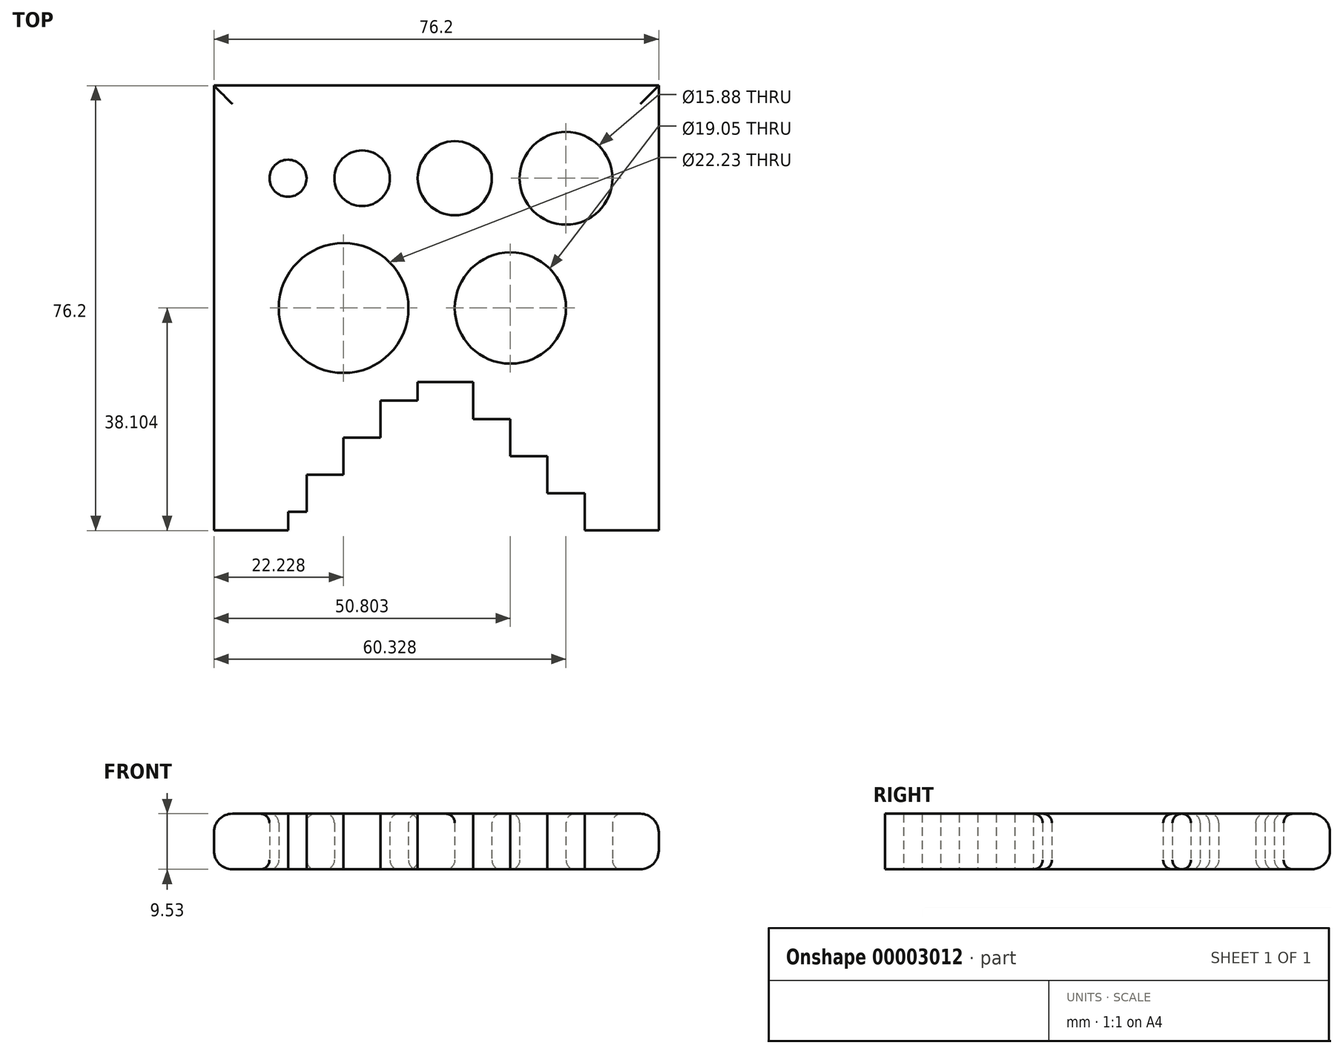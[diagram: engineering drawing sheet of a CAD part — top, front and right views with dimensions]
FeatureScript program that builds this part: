
annotation { "Feature Type Name" : "Feature", "Feature Type Description" : "" }
export const myFeature = defineFeature(function(context is Context, id is Id, definition is map)
    precondition{}
    {
        {
            var Q0;
            Q0=qCreatedBy(makeId("Top.planeOp"),FACE);
            var sketch = newSketch(context, id + "F0", { "sketchPlane" : qUnion([Q0])});
            skLineSegment(sketch, "E0.bottom", {"start": v(-53.47, 47.93) * mm, "end": v(22.73, 47.93) * mm});
            skLineSegment(sketch, "E0.top", {"start": v(-53.47, -28.27) * mm, "end": v(-40.77, -28.27) * mm});
            skLineSegment(sketch, "E0.left", {"start": v(-53.47, 47.93) * mm, "end": v(-53.47, -28.27) * mm});
            skLineSegment(sketch, "E0.right", {"start": v(22.73, 47.93) * mm, "end": v(22.73, -28.27) * mm});
            skLineSegment(sketch, "E1", {"start": v(-40.77, -25.1) * mm, "end": v(-37.6, -25.1) * mm});
            skLineSegment(sketch, "E2", {"start": v(-37.6, -18.74) * mm, "end": v(-31.24, -18.74) * mm});
            skLineSegment(sketch, "E3", {"start": v(-31.24, -12.4) * mm, "end": v(-24.9, -12.4) * mm});
            skLineSegment(sketch, "E4", {"start": v(-24.9, -6.04) * mm, "end": v(-18.54, -6.04) * mm});
            skLineSegment(sketch, "E5", {"start": v(-18.54, -2.87) * mm, "end": v(-9.02, -2.87) * mm});
            skLineSegment(sketch, "E6", {"start": v(3.68, -21.92) * mm, "end": v(10.03, -21.92) * mm});
            skLineSegment(sketch, "E7", {"start": v(-2.67, -15.57) * mm, "end": v(3.68, -15.57) * mm});
            skLineSegment(sketch, "E8", {"start": v(-9.02, -9.22) * mm, "end": v(-2.67, -9.22) * mm});
            skLineSegment(sketch, "E9", {"start": v(-18.54, -6.04) * mm, "end": v(-18.54, -2.87) * mm});
            skLineSegment(sketch, "E10", {"start": v(-24.9, -12.4) * mm, "end": v(-24.9, -6.04) * mm});
            skLineSegment(sketch, "E11", {"start": v(-31.24, -18.74) * mm, "end": v(-31.24, -12.4) * mm});
            skLineSegment(sketch, "E12", {"start": v(-37.6, -25.1) * mm, "end": v(-37.6, -18.74) * mm});
            skLineSegment(sketch, "E13", {"start": v(-40.77, -28.27) * mm, "end": v(-40.77, -25.1) * mm});
            skLineSegment(sketch, "E14", {"start": v(-9.02, -9.22) * mm, "end": v(-9.02, -2.87) * mm});
            skLineSegment(sketch, "E15", {"start": v(-2.67, -15.57) * mm, "end": v(-2.67, -9.22) * mm});
            skLineSegment(sketch, "E16", {"start": v(3.68, -21.92) * mm, "end": v(3.68, -15.57) * mm});
            skLineSegment(sketch, "E17", {"start": v(10.03, -28.27) * mm, "end": v(10.03, -21.92) * mm});
            skPoint(sketch, "E18.orphan", {"position": v(-15.37, -2.87) * mm});
            skPoint(sketch, "E19.orphan", {"position": v(-53.47, -25.1) * mm});
            skPoint(sketch, "E20.orphan", {"position": v(-53.47, -18.74) * mm});
            skPoint(sketch, "E21.orphan", {"position": v(-53.47, -12.4) * mm});
            skPoint(sketch, "E22.orphan", {"position": v(-53.47, -6.04) * mm});
            skPoint(sketch, "E23.orphan", {"position": v(22.73, -15.57) * mm});
            skPoint(sketch, "E24.orphan", {"position": v(22.73, -21.92) * mm});
            skPoint(sketch, "E25.orphan", {"position": v(22.73, -2.87) * mm});
            skPoint(sketch, "E26.orphan", {"position": v(-53.47, -2.87) * mm});
            skLineSegment(sketch, "E27.trimOffspring", {"start": v(10.03, -28.27) * mm, "end": v(22.73, -28.27) * mm});
            skLineSegment(sketch, "E28", {"start": v(-53.47, 32.06) * mm, "end": v(22.73, 32.06) * mm, "construction": true});
            skCircle(sketch, "E29", {"center": v(-40.77, 32.06) * mm, "radius": 3.18 * mm});
            skCircle(sketch, "E30", {"center": v(-28.07, 32.06) * mm, "radius": 4.76 * mm});
            skCircle(sketch, "E31", {"center": v(-12.2, 32.06) * mm, "radius": 6.35 * mm});
            skCircle(sketch, "E32", {"center": v(6.86, 32.06) * mm, "radius": 7.94 * mm});
            skLineSegment(sketch, "E33", {"start": v(22.73, 9.83) * mm, "end": v(-53.47, 9.83) * mm, "construction": true});
            skCircle(sketch, "E34", {"center": v(-2.67, 9.83) * mm, "radius": 9.53 * mm});
            skCircle(sketch, "E35", {"center": v(-31.24, 9.83) * mm, "radius": 11.11 * mm});
            skSolve(sketch);
        }
        {
            var Q0;
            {var subQ2=sQuery(id+"F0.wireOp",EDGE,"E0.right");var subQ8=sQuery(id+"F0.wireOp",EDGE,"E0.bottom");var subQ10=makeQuery(id+"F0.imprint","INTERSECT",VERTEX,{"derivedFrom":[subQ8,subQ2]});Q0=makeQuery(id+"F0.imprint","IMPRINT",FACE,{"disambiguationData":[TD([[makeQuery(id+"F0.imprint","IMPRINT",EDGE,{"disambiguationData":[TD([[subQ10,1.0]])],"derivedFrom":subQ8}),-1.0]])]});}
            var sketch = newSketch(context, id + "F1", { "sketchPlane" : qUnion([Q0])});
            skSolve(sketch);
        }
        {
            var Q0;
            Q0=makeQuery(id+"F1.imprint","IMPRINT",FACE,{"disambiguationData":[TD([[makeQuery(id+"F1.imprint","IMPRINT",EDGE,{"derivedFrom":makeQuery(id+"F0.imprint","IMPRINT",EDGE,{"derivedFrom":sQuery(id+"F0.wireOp",EDGE,"E0.bottom")})}),-1.0]])]});
            extrude(context, id + "F2", {"entities" : qUnion([Q0]), "depth" : 9.52 * mm});
        }
        {
            var Q0;
            Q0=makeQuery(id+"F2.opExtrude","CAP_EDGE",EDGE,{"disambiguationData":[OSD([sQuery(id+"F0.wireOp",EDGE,"E0.bottom")])],"isStart":false});
            var Q1;
            Q1=makeQuery(id+"F2.opExtrude","CAP_EDGE",EDGE,{"disambiguationData":[OSD([sQuery(id+"F0.wireOp",EDGE,"E0.right")])],"isStart":false});
            var Q2;
            Q2=makeQuery(id+"F2.opExtrude","CAP_EDGE",EDGE,{"disambiguationData":[OSD([sQuery(id+"F0.wireOp",EDGE,"E0.left")])],"isStart":false});
            var Q3;
            Q3=makeQuery(id+"F2.opExtrude","CAP_EDGE",EDGE,{"disambiguationData":[OSD([sQuery(id+"F0.wireOp",EDGE,"E0.right")])],"isStart":true});
            var Q4;
            Q4=makeQuery(id+"F2.opExtrude","CAP_EDGE",EDGE,{"disambiguationData":[OSD([sQuery(id+"F0.wireOp",EDGE,"E0.bottom")])],"isStart":true});
            var Q5;
            Q5=makeQuery(id+"F2.opExtrude","CAP_EDGE",EDGE,{"disambiguationData":[OSD([sQuery(id+"F0.wireOp",EDGE,"E0.left")])],"isStart":true});
            fillet(context, id + "F3", {"entities" : qUnion([Q0, Q1, Q2, Q3, Q4, Q5]), "radius" : 3.17 * mm, "tangentPropagation" : true, "allowEdgeOverflow" : false});
        }
        {
            var Q0;
            Q0=makeQuery(id+"F2.opExtrude","CAP_EDGE",EDGE,{"disambiguationData":[OSD([sQuery(id+"F0.wireOp",EDGE,"E35")])],"isStart":false});
            var Q1;
            Q1=makeQuery(id+"F2.opExtrude","CAP_EDGE",EDGE,{"disambiguationData":[OSD([sQuery(id+"F0.wireOp",EDGE,"E34")])],"isStart":false});
            var Q2;
            Q2=makeQuery(id+"F2.opExtrude","CAP_EDGE",EDGE,{"disambiguationData":[OSD([sQuery(id+"F0.wireOp",EDGE,"E32")])],"isStart":false});
            var Q3;
            Q3=makeQuery(id+"F2.opExtrude","CAP_EDGE",EDGE,{"disambiguationData":[OSD([sQuery(id+"F0.wireOp",EDGE,"E31")])],"isStart":false});
            var Q4;
            Q4=makeQuery(id+"F2.opExtrude","CAP_EDGE",EDGE,{"disambiguationData":[OSD([sQuery(id+"F0.wireOp",EDGE,"E30")])],"isStart":false});
            var Q5;
            Q5=makeQuery(id+"F2.opExtrude","CAP_EDGE",EDGE,{"disambiguationData":[OSD([sQuery(id+"F0.wireOp",EDGE,"E29")])],"isStart":false});
            var Q6;
            Q6=makeQuery(id+"F2.opExtrude","CAP_EDGE",EDGE,{"disambiguationData":[OSD([sQuery(id+"F0.wireOp",EDGE,"E34")])],"isStart":true});
            var Q7;
            Q7=makeQuery(id+"F2.opExtrude","CAP_EDGE",EDGE,{"disambiguationData":[OSD([sQuery(id+"F0.wireOp",EDGE,"E35")])],"isStart":true});
            var Q8;
            Q8=makeQuery(id+"F2.opExtrude","CAP_EDGE",EDGE,{"disambiguationData":[OSD([sQuery(id+"F0.wireOp",EDGE,"E29")])],"isStart":true});
            var Q9;
            Q9=makeQuery(id+"F2.opExtrude","CAP_EDGE",EDGE,{"disambiguationData":[OSD([sQuery(id+"F0.wireOp",EDGE,"E30")])],"isStart":true});
            var Q10;
            Q10=makeQuery(id+"F2.opExtrude","CAP_EDGE",EDGE,{"disambiguationData":[OSD([sQuery(id+"F0.wireOp",EDGE,"E31")])],"isStart":true});
            var Q11;
            Q11=makeQuery(id+"F2.opExtrude","CAP_EDGE",EDGE,{"disambiguationData":[OSD([sQuery(id+"F0.wireOp",EDGE,"E32")])],"isStart":true});
            fillet(context, id + "F4", {"entities" : qUnion([Q0, Q1, Q2, Q3, Q4, Q5, Q6, Q7, Q8, Q9, Q10, Q11]), "radius" : 1.59 * mm, "tangentPropagation" : true, "allowEdgeOverflow" : false});
        }
    });
